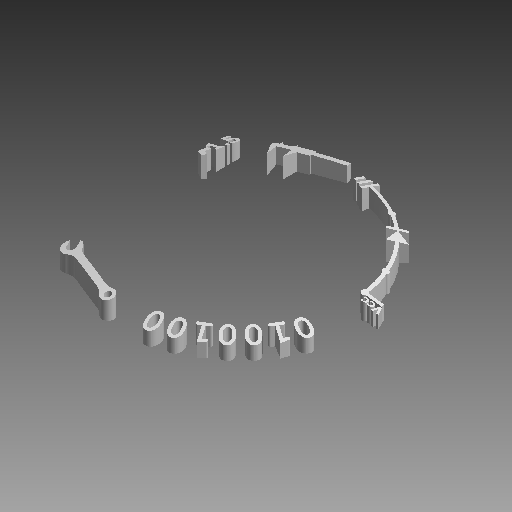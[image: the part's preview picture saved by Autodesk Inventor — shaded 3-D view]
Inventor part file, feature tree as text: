
AUTODESK INVENTOR PART (.ipt)
format: ipt  version: 2017 (Build 210142000, 142)  size: 1,119,744 bytes
history: native  units: mm (DEFAULTED — no unit token found)
features: projected_geometry x20, other x6, extrude x1, sketch x1
ambient origin geometry x8: Origin, YZ Plane, XZ Plane, XY Plane, X Axis, Y Axis, Z Axis, Center Point
bodies: Solid1 (feature_tree)
feature tree (28):
  other  "Mentor Ring.iam"
  other  "Mentor-Code text.ipt:1"
  other  "Mentor-Electrical text.ipt:1"
  other  "Team Pin Mechanical-Left Wrench.ipt:1"
  other  "Mentor-CAD text.ipt:1"
  other  "Team Pin Cad-Caliper.ipt:1"
  extrude  "Extrusion1"  Depth=10.0mm TaperAngle=0.0deg
  sketch  "Sketch1"  dims[d0=10.0mm d1=0.5mm d2=0.0mm]
  projected_geometry  "Projected Loop1"
  projected_geometry  "Projected Loop2"
  projected_geometry  "Projected Loop3"
  projected_geometry  "Projected Loop4"
  projected_geometry  "Projected Loop5"
  projected_geometry  "Projected Loop6"
  projected_geometry  "Projected Loop7"
  projected_geometry  "Projected Loop8"
  projected_geometry  "Projected Loop9"
  projected_geometry  "Projected Loop10"
  projected_geometry  "Projected Loop11"
  projected_geometry  "Projected Loop12"
  projected_geometry  "Projected Loop13"
  projected_geometry  "Projected Loop14"
  projected_geometry  "Projected Loop15"
  projected_geometry  "Projected Loop16"
  projected_geometry  "Projected Loop17"
  projected_geometry  "Projected Loop18"
  projected_geometry  "Projected Loop19"
  projected_geometry  "Projected Loop20"
